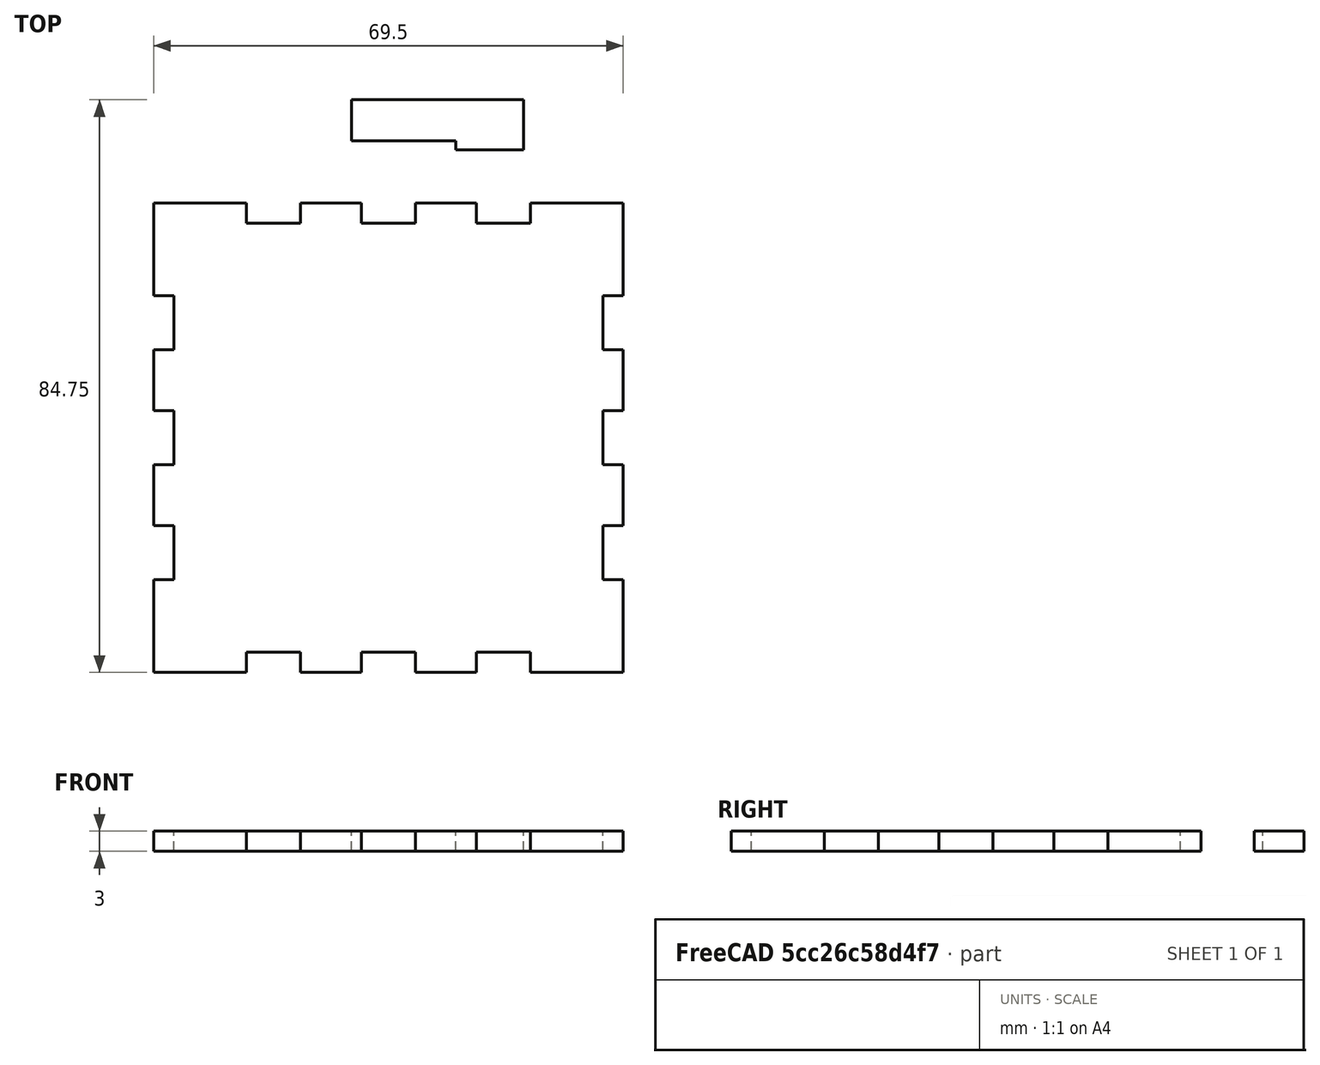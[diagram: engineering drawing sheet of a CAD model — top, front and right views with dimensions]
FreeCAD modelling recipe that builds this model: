
FCSTD DOCUMENT
Label: tea-light-base
objects: Sketcher::SketchObject×1, PartDesign::Pad×1
note: 3 computed .brp shape members not serialized (recipe doc carries the construction recipe); baked Part::Feature solids carry a one-line shape summary decoded from their .brp

FEATURE [Sketcher::SketchObject] Sketch
  sketch-geometry (52):
    g0: LineSegment StartX=-34.75 StartY=34.75 StartZ=0 EndX=-21 EndY=34.75 EndZ=0
    g1: LineSegment StartX=-21 StartY=34.75 StartZ=0 EndX=-21 EndY=31.75 EndZ=0
    g2: LineSegment StartX=-21 StartY=31.75 StartZ=0 EndX=-13 EndY=31.75 EndZ=0
    g3: LineSegment StartX=-13 StartY=31.75 StartZ=0 EndX=-13 EndY=34.75 EndZ=0
    g4: LineSegment StartX=-13 StartY=34.75 StartZ=0 EndX=-4 EndY=34.75 EndZ=0
    g5: LineSegment StartX=-4 StartY=34.75 StartZ=0 EndX=-4 EndY=31.75 EndZ=0
    g6: LineSegment StartX=-4 StartY=31.75 StartZ=0 EndX=4 EndY=31.75 EndZ=0
    g7: LineSegment StartX=4 StartY=31.75 StartZ=0 EndX=4 EndY=34.75 EndZ=0
    g8: LineSegment StartX=4 StartY=34.75 StartZ=0 EndX=13 EndY=34.75 EndZ=0
    g9: LineSegment StartX=13 StartY=34.75 StartZ=0 EndX=13 EndY=31.75 EndZ=0
    g10: LineSegment StartX=13 StartY=31.75 StartZ=0 EndX=21 EndY=31.75 EndZ=0
    g11: LineSegment StartX=21 StartY=31.75 StartZ=0 EndX=21 EndY=34.75 EndZ=0
    g12: LineSegment StartX=21 StartY=34.75 StartZ=0 EndX=34.75 EndY=34.75 EndZ=0
    g13: LineSegment StartX=34.75 StartY=34.75 StartZ=0 EndX=34.75 EndY=21 EndZ=0
    g14: LineSegment StartX=34.75 StartY=21 StartZ=0 EndX=31.75 EndY=21 EndZ=0
    g15: LineSegment StartX=31.75 StartY=21 StartZ=0 EndX=31.75 EndY=13 EndZ=0
    g16: LineSegment StartX=31.75 StartY=13 StartZ=0 EndX=34.75 EndY=13 EndZ=0
    g17: LineSegment StartX=34.75 StartY=13 StartZ=0 EndX=34.75 EndY=4 EndZ=0
    g18: LineSegment StartX=34.75 StartY=4 StartZ=0 EndX=31.75 EndY=4 EndZ=0
    g19: LineSegment StartX=31.75 StartY=4 StartZ=0 EndX=31.75 EndY=-4 EndZ=0
    g20: LineSegment StartX=31.75 StartY=-4 StartZ=0 EndX=34.75 EndY=-4 EndZ=0
    g21: LineSegment StartX=34.75 StartY=-4 StartZ=0 EndX=34.75 EndY=-13 EndZ=0
    g22: LineSegment StartX=34.75 StartY=-13 StartZ=0 EndX=31.75 EndY=-13 EndZ=0
    g23: LineSegment StartX=31.75 StartY=-13 StartZ=0 EndX=31.75 EndY=-21 EndZ=0
    g24: LineSegment StartX=31.75 StartY=-21 StartZ=0 EndX=34.75 EndY=-21 EndZ=0
    g25: LineSegment StartX=34.75 StartY=-21 StartZ=0 EndX=34.75 EndY=-34.75 EndZ=0
    g26: LineSegment StartX=34.75 StartY=-34.75 StartZ=0 EndX=21 EndY=-34.75 EndZ=0
    g27: LineSegment StartX=21 StartY=-34.75 StartZ=0 EndX=21 EndY=-31.75 EndZ=0
    g28: LineSegment StartX=21 StartY=-31.75 StartZ=0 EndX=13 EndY=-31.75 EndZ=0
    g29: LineSegment StartX=13 StartY=-31.75 StartZ=0 EndX=13 EndY=-34.75 EndZ=0
    g30: LineSegment StartX=13 StartY=-34.75 StartZ=0 EndX=4 EndY=-34.75 EndZ=0
    g31: LineSegment StartX=4 StartY=-34.75 StartZ=0 EndX=4 EndY=-31.75 EndZ=0
    g32: LineSegment StartX=4 StartY=-31.75 StartZ=0 EndX=-4 EndY=-31.75 EndZ=0
    g33: LineSegment StartX=-4 StartY=-31.75 StartZ=0 EndX=-4 EndY=-34.75 EndZ=0
    g34: LineSegment StartX=-4 StartY=-34.75 StartZ=0 EndX=-13 EndY=-34.75 EndZ=0
    g35: LineSegment StartX=-13 StartY=-34.75 StartZ=0 EndX=-13 EndY=-31.75 EndZ=0
    g36: LineSegment StartX=-13 StartY=-31.75 StartZ=0 EndX=-21 EndY=-31.75 EndZ=0
    g37: LineSegment StartX=-21 StartY=-31.75 StartZ=0 EndX=-21 EndY=-34.75 EndZ=0
    g38: LineSegment StartX=-21 StartY=-34.75 StartZ=0 EndX=-34.75 EndY=-34.75 EndZ=0
    g39: LineSegment StartX=-34.75 StartY=-34.75 StartZ=0 EndX=-34.75 EndY=-21 EndZ=0
    g40: LineSegment StartX=-34.75 StartY=-21 StartZ=0 EndX=-31.75 EndY=-21 EndZ=0
    g41: LineSegment StartX=-31.75 StartY=-21 StartZ=0 EndX=-31.75 EndY=-13 EndZ=0
    g42: LineSegment StartX=-31.75 StartY=-13 StartZ=0 EndX=-34.75 EndY=-13 EndZ=0
    g43: LineSegment StartX=-34.75 StartY=-13 StartZ=0 EndX=-34.75 EndY=-4 EndZ=0
    g44: LineSegment StartX=-34.75 StartY=-4 StartZ=0 EndX=-31.75 EndY=-4 EndZ=0
    g45: LineSegment StartX=-31.75 StartY=-4 StartZ=0 EndX=-31.75 EndY=4 EndZ=0
    g46: LineSegment StartX=-31.75 StartY=4 StartZ=0 EndX=-34.75 EndY=4 EndZ=0
    g47: LineSegment StartX=-34.75 StartY=4 StartZ=0 EndX=-34.75 EndY=13 EndZ=0
    g48: LineSegment StartX=-34.75 StartY=13 StartZ=0 EndX=-31.75 EndY=13 EndZ=0
    g49: LineSegment StartX=-31.75 StartY=13 StartZ=0 EndX=-31.75 EndY=21 EndZ=0
    g50: LineSegment StartX=-31.75 StartY=21 StartZ=0 EndX=-34.75 EndY=21 EndZ=0
    g51: LineSegment StartX=-34.75 StartY=21 StartZ=0 EndX=-34.75 EndY=34.75 EndZ=0
  constraints (156):
    c: Horizontal(g0)
    c: Coincident(g0,g1)
    c: Vertical(g1)
    c: Coincident(g1,g2)
    c: Horizontal(g2)
    c: Coincident(g2,g3)
    c: Vertical(g3)
    c: Coincident(g3,g4)
    c: Coincident(g4,g5)
    c: Coincident(g5,g6)
    c: Horizontal(g6)
    c: Coincident(g6,g7)
    c: Vertical(g7)
    c: Coincident(g7,g8)
    c: Horizontal(g8)
    c: Coincident(g8,g9)
    c: Vertical(g9)
    c: Coincident(g9,g10)
    c: Horizontal(g10)
    c: Coincident(g10,g11)
    c: Vertical(g11)
    c: Coincident(g11,g12)
    c: Horizontal(g12)
    c: Coincident(g12,g13)
    c: Vertical(g13)
    c: Coincident(g13,g14)
    c: Horizontal(g14)
    c: Coincident(g14,g15)
    c: Vertical(g15)
    c: Coincident(g15,g16)
    c: Coincident(g16,g17)
    c: Coincident(g17,g18)
    c: Coincident(g18,g19)
    c: Coincident(g19,g20)
    c: Coincident(g20,g21)
    c: Vertical(g21)
    c: Coincident(g21,g22)
    c: Coincident(g22,g23)
    c: Vertical(g23)
    c: Coincident(g23,g24)
    c: Horizontal(g24)
    c: Coincident(g24,g25)
    c: Vertical(g25)
    c: Coincident(g25,g26)
    c: Horizontal(g26)
    c: Coincident(g26,g27)
    c: Vertical(g27)
    c: Coincident(g27,g28)
    c: Horizontal(g28)
    c: Coincident(g28,g29)
    c: Vertical(g29)
    c: Coincident(g29,g30)
    c: Coincident(g30,g31)
    c: Coincident(g31,g32)
    c: Horizontal(g32)
    c: Coincident(g32,g33)
    c: Coincident(g33,g34)
    c: Coincident(g34,g35)
    c: Vertical(g35)
    c: Coincident(g35,g36)
    c: Coincident(g36,g37)
    c: Coincident(g37,g38)
    c: Horizontal(g38)
    c: Coincident(g38,g39)
    c: Vertical(g39)
    c: Coincident(g39,g40)
    c: Coincident(g40,g41)
    c: Coincident(g41,g42)
    c: Coincident(g42,g43)
    c: Coincident(g43,g44)
    c: Horizontal(g44)
    c: Coincident(g44,g45)
    c: Coincident(g45,g46)
    c: Coincident(g46,g47)
    c: Coincident(g47,g48)
    c: Horizontal(g48)
    c: Coincident(g48,g49)
    c: Vertical(g49)
    c: Coincident(g49,g50)
    c: Coincident(g50,g51)
    c: Vertical(g51)
    c: Coincident(g51,g0)
    c: Equal(g50,g48)
    c: Equal(g48,g46)
    c: Equal(g46,g44)
    c: Equal(g44,g42)
    c: Equal(g42,g40)
    c: Horizontal(g42)
    c: Horizontal(g46)
    c: Horizontal(g40)
    c: Vertical(g47)
    c: Vertical(g43)
    c: Vertical(g41)
    c: Vertical(g37)
    c: Equal(g43,g47)
    c: Equal(g47,g4)
    c: Equal(g4,g8)
    c: Equal(g8,g17)
    c: Equal(g17,g21)
    c: Equal(g21,g30)
    c: Equal(g30,g34)
    c: DistanceX(g50) = -3
    c: Vertical(g33)
    c: Vertical(g31)
    c: Horizontal(g36)
    c: Horizontal(g34)
    c: Horizontal(g30)
    c: Equal(g0,g51)
    c: Equal(g51,g39)
    c: Equal(g39,g38)
    c: Equal(g38,g26)
    c: Equal(g26,g25)
    c: Equal(g25,g12)
    c: Equal(g12,g13)
    c: Horizontal(g4)
    c: Vertical(g5)
    c: Horizontal(g16)
    c: Vertical(g19)
    c: Horizontal(g20)
    c: Horizontal(g18)
    c: Equal(g40,g37)
    c: Equal(g37,g35)
    c: Equal(g35,g33)
    c: Equal(g33,g31)
    c: Equal(g31,g29)
    c: Equal(g29,g27)
    c: Equal(g27,g24)
    c: Equal(g24,g22)
    c: Equal(g22,g20)
    c: Equal(g20,g18)
    c: Equal(g18,g16)
    c: Equal(g16,g14)
    c: Vertical(g17)
    c: Horizontal(g50)
    c: Equal(g1,g3)
    c: Equal(g3,g5)
    c: Equal(g5,g7)
    c: Equal(g7,g9)
    c: Equal(g9,g11)
    c: Equal(g11,g14)
    c: Equal(g49,g2)
    c: Equal(g2,g6)
    c: Equal(g6,g10)
    c: Equal(g10,g15)
    c: Equal(g15,g19)
    c: Equal(g19,g23)
    c: Equal(g23,g28)
    c: Equal(g28,g32)
    c: Equal(g32,g36)
    c: Equal(g36,g41)
    c: Equal(g41,g45)
    c: Symmetric(g44,g45,g-1)
    c: DistanceY(g10,g27) = -63.5
    c: Symmetric(g5,g6,g-2)
    c: DistanceY(g49) = 8
    c: DistanceY(g47) = 9
FEATURE [PartDesign::Pad] Pad
  Length = 3
  Length2 = 100
  Sketch = -> Sketch
  Type = 0
